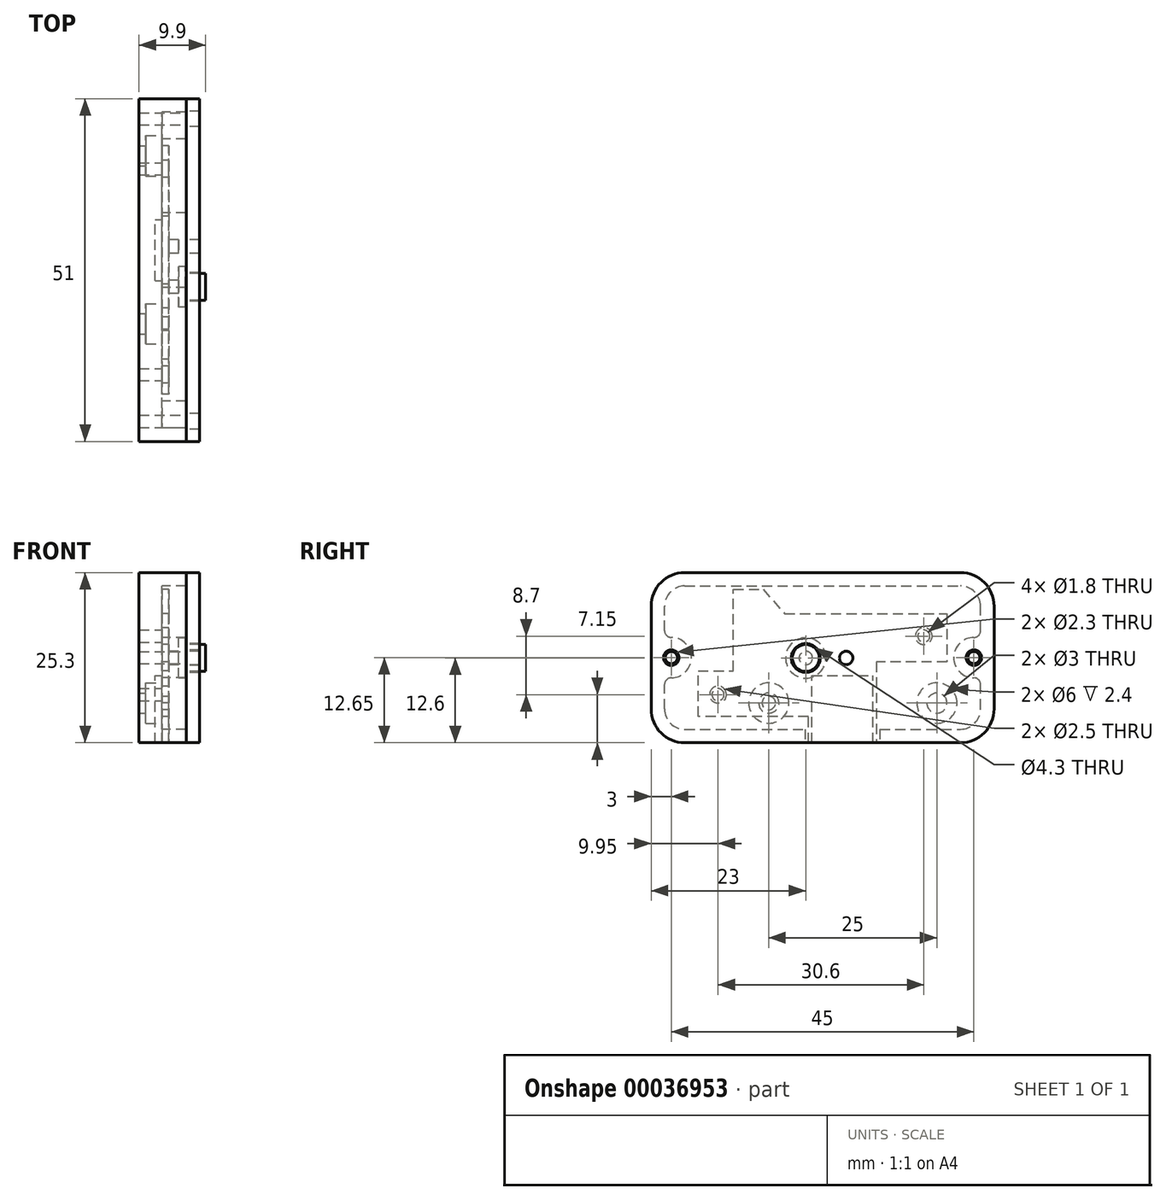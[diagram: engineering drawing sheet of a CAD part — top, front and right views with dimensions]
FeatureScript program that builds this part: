
annotation { "Feature Type Name" : "Feature", "Feature Type Description" : "" }
export const myFeature = defineFeature(function(context is Context, id is Id, definition is map)
    precondition{}
    {
        {
            var Q0;
            Q0=qCreatedBy(makeId("Right.planeOp"),FACE);
            var sketch = newSketch(context, id + "F0", { "sketchPlane" : qUnion([Q0])});
            skLineSegment(sketch, "E0", {"start": v(0, 0) * mm, "end": v(0, 6.8) * mm});
            skLineSegment(sketch, "E1", {"start": v(0, 6.8) * mm, "end": v(5.25, 6.8) * mm});
            skLineSegment(sketch, "E2", {"start": v(5.25, 6.8) * mm, "end": v(5.25, 18.9) * mm});
            skLineSegment(sketch, "E3", {"start": v(5.25, 18.9) * mm, "end": v(9.65, 18.9) * mm});
            skLineSegment(sketch, "E4", {"start": v(9.65, 18.9) * mm, "end": v(12.85, 15.3) * mm});
            skLineSegment(sketch, "E5", {"start": v(12.85, 15.3) * mm, "end": v(37, 15.3) * mm});
            skLineSegment(sketch, "E6", {"start": v(37, 15.3) * mm, "end": v(37, 8.1) * mm});
            skLineSegment(sketch, "E7", {"start": v(37, 8.1) * mm, "end": v(26.5, 8.1) * mm});
            skLineSegment(sketch, "E8", {"start": v(26.5, 8.1) * mm, "end": v(26.5, -3.9) * mm});
            skLineSegment(sketch, "E9", {"start": v(26.5, -3.9) * mm, "end": v(16.4, -3.9) * mm});
            skLineSegment(sketch, "E10", {"start": v(16.4, -3.9) * mm, "end": v(16.4, 0) * mm});
            skLineSegment(sketch, "E11", {"start": v(16.4, 0) * mm, "end": v(0, 0) * mm});
            skCircle(sketch, "E12", {"center": v(2.95, 3.25) * mm, "radius": 1.25 * mm});
            skCircle(sketch, "E13", {"center": v(10.5, 2) * mm, "radius": 1 * mm});
            skCircle(sketch, "E14", {"center": v(33.55, 11.95) * mm, "radius": 1.25 * mm});
            skSolve(sketch);
        }
        {
            var Q0;
            Q0 = qSketchRegion(id + "F0", true);
            extrude(context, id + "F1", {"entities" : qUnion([Q0]), "depth" : 1 * mm});
        }
        {
            var Q0;
            Q0=makeQuery(id+"F1.opExtrude","CAP_FACE",FACE,{"disambiguationData":[OSD([sQuery(id+"F0.wireOp",EDGE,"E0"),sQuery(id+"F0.wireOp",EDGE,"E1"),sQuery(id+"F0.wireOp",EDGE,"E2"),sQuery(id+"F0.wireOp",EDGE,"E3"),sQuery(id+"F0.wireOp",EDGE,"E4"),sQuery(id+"F0.wireOp",EDGE,"E5"),sQuery(id+"F0.wireOp",EDGE,"E6"),sQuery(id+"F0.wireOp",EDGE,"E7"),sQuery(id+"F0.wireOp",EDGE,"E8"),sQuery(id+"F0.wireOp",EDGE,"E9"),sQuery(id+"F0.wireOp",EDGE,"E10"),sQuery(id+"F0.wireOp",EDGE,"E11"),sQuery(id+"F0.wireOp",EDGE,"E12"),sQuery(id+"F0.wireOp",EDGE,"E13"),sQuery(id+"F0.wireOp",EDGE,"E14")])],"isStart":false});
            var sketch = newSketch(context, id + "F2", { "sketchPlane" : qUnion([Q0])});
            skCircle(sketch, "E15", {"center": v(16, 8.7) * mm, "radius": 1 * mm});
            skCircle(sketch, "E16", {"center": v(22, 8.7) * mm, "radius": 1 * mm});
            skSolve(sketch);
        }
        {
            var Q0;
            Q0 = qSketchRegion(id + "F2", true);
            extrude(context, id + "F3", {"entities" : qUnion([Q0]), "operationType" : NewBodyOperationType.ADD, "depth" : 1.5 * mm});
        }
        {
            var Q0;
            Q0=qCreatedBy(makeId("Right.planeOp"),FACE);
            var sketch = newSketch(context, id + "F4", { "sketchPlane" : qUnion([Q0])});
            skCircle(sketch, "E17.0", {"center": v(10.5, 2) * mm, "radius": 1 * mm});
            skCircle(sketch, "E18", {"center": v(10.5, 2) * mm, "radius": 1.5 * mm});
            skCircle(sketch, "E19", {"center": v(35.5, 2) * mm, "radius": 1.5 * mm});
            skLineSegment(sketch, "E20.bottom", {"start": v(-2, -3.9) * mm, "end": v(39, -3.9) * mm});
            skLineSegment(sketch, "E20.top", {"start": v(-2, 21.4) * mm, "end": v(39, 21.4) * mm});
            skLineSegment(sketch, "E20.left", {"start": v(-7, 1.1) * mm, "end": v(-7, 16.4) * mm});
            skLineSegment(sketch, "E20.right", {"start": v(44, 1.1) * mm, "end": v(44, 16.4) * mm});
            skPoint(sketch, "E21.visualSharp", {"position": v(-7, 21.4) * mm});
            skArc(sketch, "E21.filletArc", {"start": v(-2, 21.4) * mm, "mid": v(-5.54, 19.94) * mm, "end": v(-7, 16.4) * mm});
            skPoint(sketch, "E22.visualSharp", {"position": v(44, 21.4) * mm});
            skArc(sketch, "E22.filletArc", {"start": v(44, 16.4) * mm, "mid": v(42.54, 19.94) * mm, "end": v(39, 21.4) * mm});
            skPoint(sketch, "E23.visualSharp", {"position": v(44, -3.9) * mm});
            skArc(sketch, "E23.filletArc", {"start": v(39, -3.9) * mm, "mid": v(42.54, -2.44) * mm, "end": v(44, 1.1) * mm});
            skPoint(sketch, "E24.visualSharp", {"position": v(-7, -3.9) * mm});
            skArc(sketch, "E24.filletArc", {"start": v(-7, 1.1) * mm, "mid": v(-5.54, -2.44) * mm, "end": v(-2, -3.9) * mm});
            skSolve(sketch);
        }
        {
            var Q0;
            Q0=makeQuery(id+"F4.imprint","IMPRINT",FACE,{"disambiguationData":[TD([[makeQuery(id+"F4.imprint","IMPRINT",EDGE,{"derivedFrom":sQuery(id+"F4.wireOp",EDGE,"E18")}),-1.0]])]});
            extrude(context, id + "F5", {"entities" : qUnion([Q0]), "oppositeDirection" : true, "depth" : 3.4 * mm});
        }
        {
            var Q0;
            {var subQ0=sQuery(id+"F4.wireOp",EDGE,"E19");var subQ1=sQuery(id+"F4.wireOp",EDGE,"E20.bottom");var subQ2=sQuery(id+"F4.wireOp",EDGE,"E20.top");var subQ3=sQuery(id+"F4.wireOp",EDGE,"E20.left");var subQ4=sQuery(id+"F4.wireOp",EDGE,"E20.right");var subQ5=sQuery(id+"F4.wireOp",EDGE,"E21.filletArc");var subQ6=sQuery(id+"F4.wireOp",EDGE,"E22.filletArc");var subQ7=sQuery(id+"F4.wireOp",EDGE,"E23.filletArc");var subQ8=sQuery(id+"F4.wireOp",EDGE,"E24.filletArc");Q0=makeQuery(id+"F5.boolean.opBoolean","SPLIT",FACE,{"disambiguationData":[TD([makeQuery(id+"F1.opExtrude","SWEPT_FACE",FACE,{"disambiguationData":[OSD([sQuery(id+"F0.wireOp",EDGE,"E0")])]})])],"derivedFrom":makeQuery(id+"F5.opExtrude","CAP_FACE",FACE,{"disambiguationData":[OSD([sQuery(id+"F4.wireOp",EDGE,"E18"),subQ0,subQ1,subQ2,subQ3,subQ4,subQ5,subQ6,subQ7,subQ8])],"isStart":true})});}
            var sketch = newSketch(context, id + "F6", { "sketchPlane" : qUnion([Q0])});
            skCircle(sketch, "E25", {"center": v(35.5, 2) * mm, "radius": 3 * mm});
            skCircle(sketch, "E26", {"center": v(10.5, 2) * mm, "radius": 3 * mm});
            skSolve(sketch);
        }
        {
            var Q0;
            Q0 = qSketchRegion(id + "F6", true);
            extrude(context, id + "F7", {"entities" : qUnion([Q0]), "operationType" : NewBodyOperationType.REMOVE, "oppositeDirection" : true, "depth" : 2.4 * mm});
        }
        {
            var Q0;
            Q0=makeQuery(id+"F5.opExtrude","CAP_FACE",FACE,{"disambiguationData":[OSD([sQuery(id+"F4.wireOp",EDGE,"E18"),sQuery(id+"F4.wireOp",EDGE,"E19"),sQuery(id+"F4.wireOp",EDGE,"E20.bottom"),sQuery(id+"F4.wireOp",EDGE,"E20.top"),sQuery(id+"F4.wireOp",EDGE,"E20.left"),sQuery(id+"F4.wireOp",EDGE,"E20.right"),sQuery(id+"F4.wireOp",EDGE,"E21.filletArc"),sQuery(id+"F4.wireOp",EDGE,"E22.filletArc"),sQuery(id+"F4.wireOp",EDGE,"E23.filletArc"),sQuery(id+"F4.wireOp",EDGE,"E24.filletArc")])],"isStart":true});
            var sketch = newSketch(context, id + "F8", { "sketchPlane" : qUnion([Q0])});
            skLineSegment(sketch, "E27.bottom", {"start": v(16.9, -3.9) * mm, "end": v(26, -3.9) * mm});
            skLineSegment(sketch, "E27.top", {"start": v(16.9, 6.1) * mm, "end": v(26, 6.1) * mm});
            skLineSegment(sketch, "E27.left", {"start": v(16.9, -3.9) * mm, "end": v(16.9, 6.1) * mm});
            skLineSegment(sketch, "E27.right", {"start": v(26, -3.9) * mm, "end": v(26, 6.1) * mm});
            skSolve(sketch);
        }
        {
            var Q0;
            Q0 = qSketchRegion(id + "F8", true);
            extrude(context, id + "F9", {"entities" : qUnion([Q0]), "operationType" : NewBodyOperationType.REMOVE, "oppositeDirection" : true, "depth" : 1 * mm});
        }
        {
            var Q0;
            Q0=makeQuery(id+"F5.opExtrude","CAP_FACE",FACE,{"disambiguationData":[OSD([sQuery(id+"F4.wireOp",EDGE,"E18"),sQuery(id+"F4.wireOp",EDGE,"E19"),sQuery(id+"F4.wireOp",EDGE,"E20.bottom"),sQuery(id+"F4.wireOp",EDGE,"E20.top"),sQuery(id+"F4.wireOp",EDGE,"E20.left"),sQuery(id+"F4.wireOp",EDGE,"E20.right"),sQuery(id+"F4.wireOp",EDGE,"E21.filletArc"),sQuery(id+"F4.wireOp",EDGE,"E22.filletArc"),sQuery(id+"F4.wireOp",EDGE,"E23.filletArc"),sQuery(id+"F4.wireOp",EDGE,"E24.filletArc")])],"isStart":true});
            var sketch = newSketch(context, id + "F10", { "sketchPlane" : qUnion([Q0])});
            skCircle(sketch, "E28", {"center": v(33.55, 11.95) * mm, "radius": 0.9 * mm});
            skCircle(sketch, "E29", {"center": v(2.95, 3.25) * mm, "radius": 0.9 * mm});
            skSolve(sketch);
        }
        {
            var Q0;
            Q0 = qSketchRegion(id + "F10", true);
            extrude(context, id + "F11", {"entities" : qUnion([Q0]), "operationType" : NewBodyOperationType.REMOVE, "endBound" : BoundingType.THROUGH_ALL, "oppositeDirection" : true, "depth" : 25 * mm});
        }
        {
            var Q0;
            Q0=makeQuery(id+"F5.opExtrude","CAP_FACE",FACE,{"disambiguationData":[OSD([sQuery(id+"F4.wireOp",EDGE,"E18"),sQuery(id+"F4.wireOp",EDGE,"E19"),sQuery(id+"F4.wireOp",EDGE,"E20.bottom"),sQuery(id+"F4.wireOp",EDGE,"E20.top"),sQuery(id+"F4.wireOp",EDGE,"E20.left"),sQuery(id+"F4.wireOp",EDGE,"E20.right"),sQuery(id+"F4.wireOp",EDGE,"E21.filletArc"),sQuery(id+"F4.wireOp",EDGE,"E22.filletArc"),sQuery(id+"F4.wireOp",EDGE,"E23.filletArc"),sQuery(id+"F4.wireOp",EDGE,"E24.filletArc")])],"isStart":true});
            var sketch = newSketch(context, id + "F12", { "sketchPlane" : qUnion([Q0])});
            skLineSegment(sketch, "E30.0", {"start": v(-2, 21.4) * mm, "end": v(39, 21.4) * mm});
            skArc(sketch, "E31.0", {"start": v(44, 16.4) * mm, "mid": v(42.54, 19.94) * mm, "end": v(39, 21.4) * mm});
            skLineSegment(sketch, "E32.0", {"start": v(44, 1.1) * mm, "end": v(44, 16.4) * mm});
            skArc(sketch, "E33.0", {"start": v(39, -3.9) * mm, "mid": v(42.54, -2.44) * mm, "end": v(44, 1.1) * mm});
            skLineSegment(sketch, "E34.0", {"start": v(26, -3.9) * mm, "end": v(39, -3.9) * mm});
            skLineSegment(sketch, "E35.0", {"start": v(-2, -3.9) * mm, "end": v(16.9, -3.9) * mm});
            skArc(sketch, "E36.0", {"start": v(-7, 1.1) * mm, "mid": v(-5.54, -2.44) * mm, "end": v(-2, -3.9) * mm});
            skLineSegment(sketch, "E37.0", {"start": v(-7, 1.1) * mm, "end": v(-7, 16.4) * mm});
            skArc(sketch, "E38.0", {"start": v(-2, 21.4) * mm, "mid": v(-5.54, 19.94) * mm, "end": v(-7, 16.4) * mm});
            skLineSegment(sketch, "E39.0", {"start": v(27, -1.9) * mm, "end": v(39, -1.9) * mm});
            skArc(sketch, "E39.1", {"start": v(39, -1.9) * mm, "mid": v(41.12, -1.02) * mm, "end": v(42, 1.1) * mm});
            skLineSegment(sketch, "E39.2", {"start": v(42, 1.1) * mm, "end": v(42, 4.75) * mm});
            skArc(sketch, "E39.3", {"start": v(42, 16.4) * mm, "mid": v(41.12, 18.52) * mm, "end": v(39, 19.4) * mm});
            skLineSegment(sketch, "E39.4", {"start": v(-2, 19.4) * mm, "end": v(39, 19.4) * mm});
            skArc(sketch, "E39.5", {"start": v(-2, 19.4) * mm, "mid": v(-4.12, 18.52) * mm, "end": v(-5, 16.4) * mm});
            skLineSegment(sketch, "E39.6", {"start": v(-5, 1.1) * mm, "end": v(-5, 4.75) * mm});
            skArc(sketch, "E39.7", {"start": v(-5, 1.1) * mm, "mid": v(-4.12, -1.02) * mm, "end": v(-2, -1.9) * mm});
            skLineSegment(sketch, "E39.8", {"start": v(-2, -1.9) * mm, "end": v(15.9, -1.9) * mm});
            skLineSegment(sketch, "E40", {"start": v(15.9, -1.9) * mm, "end": v(15.9, -3.9) * mm});
            skLineSegment(sketch, "E41", {"start": v(27, -1.9) * mm, "end": v(27, -3.9) * mm});
            skArc(sketch, "E42", {"start": v(-4, 5.75) * mm, "mid": v(-1, 8.75) * mm, "end": v(-4, 11.75) * mm});
            skArc(sketch, "E43", {"start": v(-5, 12.75) * mm, "mid": v(-4.7, 12.04) * mm, "end": v(-4, 11.75) * mm});
            skArc(sketch, "E44", {"start": v(-4, 5.75) * mm, "mid": v(-4.7, 5.46) * mm, "end": v(-5, 4.75) * mm});
            skPoint(sketch, "E45", {"position": v(-7, 8.75) * mm});
            skLineSegment(sketch, "E46.trimOffspring", {"start": v(-5, 12.75) * mm, "end": v(-5, 16.4) * mm});
            skArc(sketch, "E47", {"start": v(41, 11.75) * mm, "mid": v(38, 8.75) * mm, "end": v(41, 5.75) * mm});
            skArc(sketch, "E48", {"start": v(41, 11.75) * mm, "mid": v(41.7, 12.04) * mm, "end": v(42, 12.75) * mm});
            skArc(sketch, "E49", {"start": v(42, 4.75) * mm, "mid": v(41.7, 5.46) * mm, "end": v(41, 5.75) * mm});
            skPoint(sketch, "E50", {"position": v(44, 8.75) * mm});
            skLineSegment(sketch, "E51.trimOffspring", {"start": v(42, 12.75) * mm, "end": v(42, 16.4) * mm});
            skSolve(sketch);
        }
        {
            var Q0;
            Q0 = qSketchRegion(id + "F12", true);
            extrude(context, id + "F13", {"entities" : qUnion([Q0]), "operationType" : NewBodyOperationType.ADD, "depth" : 3.6 * mm});
        }
        {
            var Q0;
            Q0=makeQuery(id+"F13.opExtrude","CAP_FACE",FACE,{"disambiguationData":[OSD([sQuery(id+"F12.wireOp",EDGE,"E30.0"),sQuery(id+"F12.wireOp",EDGE,"E31.0"),sQuery(id+"F12.wireOp",EDGE,"E32.0"),sQuery(id+"F12.wireOp",EDGE,"E33.0"),sQuery(id+"F12.wireOp",EDGE,"E34.0"),sQuery(id+"F12.wireOp",EDGE,"E35.0"),sQuery(id+"F12.wireOp",EDGE,"E36.0"),sQuery(id+"F12.wireOp",EDGE,"E37.0"),sQuery(id+"F12.wireOp",EDGE,"E38.0"),sQuery(id+"F12.wireOp",EDGE,"E39.0"),sQuery(id+"F12.wireOp",EDGE,"E39.1"),sQuery(id+"F12.wireOp",EDGE,"E39.2"),sQuery(id+"F12.wireOp",EDGE,"E39.3"),sQuery(id+"F12.wireOp",EDGE,"E39.4"),sQuery(id+"F12.wireOp",EDGE,"E39.5"),sQuery(id+"F12.wireOp",EDGE,"E39.6"),sQuery(id+"F12.wireOp",EDGE,"E39.7"),sQuery(id+"F12.wireOp",EDGE,"E39.8"),sQuery(id+"F12.wireOp",EDGE,"E40"),sQuery(id+"F12.wireOp",EDGE,"E41"),sQuery(id+"F12.wireOp",EDGE,"E42"),sQuery(id+"F12.wireOp",EDGE,"E43"),sQuery(id+"F12.wireOp",EDGE,"E44"),sQuery(id+"F12.wireOp",EDGE,"E46.trimOffspring"),sQuery(id+"F12.wireOp",EDGE,"E47"),sQuery(id+"F12.wireOp",EDGE,"E48"),sQuery(id+"F12.wireOp",EDGE,"E49"),sQuery(id+"F12.wireOp",EDGE,"E51.trimOffspring")])],"isStart":false});
            var sketch = newSketch(context, id + "F14", { "sketchPlane" : qUnion([Q0])});
            skCircle(sketch, "E52", {"center": v(-4, 8.75) * mm, "radius": 0.9 * mm});
            skCircle(sketch, "E53", {"center": v(41, 8.75) * mm, "radius": 0.9 * mm});
            skSolve(sketch);
        }
        {
            var Q0;
            Q0 = qSketchRegion(id + "F14", true);
            extrude(context, id + "F15", {"entities" : qUnion([Q0]), "operationType" : NewBodyOperationType.REMOVE, "endBound" : BoundingType.THROUGH_ALL, "oppositeDirection" : true, "depth" : 25 * mm});
        }
        {
            var Q0;
            Q0=makeQuery(id+"F13.opExtrude","CAP_FACE",FACE,{"disambiguationData":[OSD([sQuery(id+"F12.wireOp",EDGE,"E30.0"),sQuery(id+"F12.wireOp",EDGE,"E31.0"),sQuery(id+"F12.wireOp",EDGE,"E32.0"),sQuery(id+"F12.wireOp",EDGE,"E33.0"),sQuery(id+"F12.wireOp",EDGE,"E34.0"),sQuery(id+"F12.wireOp",EDGE,"E35.0"),sQuery(id+"F12.wireOp",EDGE,"E36.0"),sQuery(id+"F12.wireOp",EDGE,"E37.0"),sQuery(id+"F12.wireOp",EDGE,"E38.0"),sQuery(id+"F12.wireOp",EDGE,"E39.0"),sQuery(id+"F12.wireOp",EDGE,"E39.1"),sQuery(id+"F12.wireOp",EDGE,"E39.2"),sQuery(id+"F12.wireOp",EDGE,"E39.3"),sQuery(id+"F12.wireOp",EDGE,"E39.4"),sQuery(id+"F12.wireOp",EDGE,"E39.5"),sQuery(id+"F12.wireOp",EDGE,"E39.6"),sQuery(id+"F12.wireOp",EDGE,"E39.7"),sQuery(id+"F12.wireOp",EDGE,"E39.8"),sQuery(id+"F12.wireOp",EDGE,"E40"),sQuery(id+"F12.wireOp",EDGE,"E41"),sQuery(id+"F12.wireOp",EDGE,"E42"),sQuery(id+"F12.wireOp",EDGE,"E43"),sQuery(id+"F12.wireOp",EDGE,"E44"),sQuery(id+"F12.wireOp",EDGE,"417ee6bc-ae09-479d-8291-56012da80ed6"),sQuery(id+"F12.wireOp",EDGE,"E46.trimOffspring"),sQuery(id+"F12.wireOp",EDGE,"E47"),sQuery(id+"F12.wireOp",EDGE,"E48"),sQuery(id+"F12.wireOp",EDGE,"E49"),sQuery(id+"F12.wireOp",EDGE,"E51.trimOffspring"),sQuery(id+"F12.wireOp",EDGE,"95503bac-c556-4579-a5fb-9d73f4b7cb5d")])],"isStart":false});
            var sketch = newSketch(context, id + "F16", { "sketchPlane" : qUnion([Q0])});
            skLineSegment(sketch, "E54.0", {"start": v(-7, 1.1) * mm, "end": v(-7, 16.4) * mm});
            skArc(sketch, "E54.1", {"start": v(-2, 21.4) * mm, "mid": v(-5.54, 19.94) * mm, "end": v(-7, 16.4) * mm});
            skLineSegment(sketch, "E54.2", {"start": v(-2, 21.4) * mm, "end": v(39, 21.4) * mm});
            skArc(sketch, "E54.3", {"start": v(44, 16.4) * mm, "mid": v(42.54, 19.94) * mm, "end": v(39, 21.4) * mm});
            skLineSegment(sketch, "E54.4", {"start": v(44, 1.1) * mm, "end": v(44, 16.4) * mm});
            skArc(sketch, "E54.5", {"start": v(39, -3.9) * mm, "mid": v(42.54, -2.44) * mm, "end": v(44, 1.1) * mm});
            skLineSegment(sketch, "E54.6", {"start": v(27, -3.9) * mm, "end": v(39, -3.9) * mm});
            skLineSegment(sketch, "E54.7", {"start": v(-2, -3.9) * mm, "end": v(15.9, -3.9) * mm});
            skArc(sketch, "E54.8", {"start": v(-7, 1.1) * mm, "mid": v(-5.54, -2.44) * mm, "end": v(-2, -3.9) * mm});
            skLineSegment(sketch, "E55", {"start": v(15.9, -3.9) * mm, "end": v(27, -3.9) * mm});
            skCircle(sketch, "E56", {"center": v(-4, 8.75) * mm, "radius": 1.15 * mm});
            skCircle(sketch, "E57", {"center": v(41, 8.75) * mm, "radius": 1.15 * mm});
            skCircle(sketch, "E58.0", {"center": v(16, 8.7) * mm, "radius": 1 * mm});
            skCircle(sketch, "E59", {"center": v(16, 8.7) * mm, "radius": 2.15 * mm});
            skCircle(sketch, "E60.0", {"center": v(22, 8.7) * mm, "radius": 1 * mm});
            skSolve(sketch);
        }
        {
            var Q0;
            Q0 = qSketchRegion(id + "F16", true);
            extrude(context, id + "F17", {"entities" : qUnion([Q0]), "depth" : 2 * mm});
        }
        {
            var Q0;
            Q0=makeQuery(id+"F3.opExtrude","CAP_FACE",FACE,{"disambiguationData":[OSD([sQuery(id+"F2.wireOp",EDGE,"E15")])],"isStart":false});
            var sketch = newSketch(context, id + "F18", { "sketchPlane" : qUnion([Q0])});
            skCircle(sketch, "E61", {"center": v(16, 8.7) * mm, "radius": 3 * mm});
            skSolve(sketch);
        }
        {
            var Q0;
            Q0 = qSketchRegion(id + "F18", true);
            extrude(context, id + "F19", {"entities" : qUnion([Q0]), "depth" : 1 * mm});
        }
        {
            var Q0;
            Q0=makeQuery(id+"F19.opExtrude","CAP_FACE",FACE,{"disambiguationData":[OSD([sQuery(id+"F18.wireOp",EDGE,"E61")])],"isStart":false});
            var sketch = newSketch(context, id + "F20", { "sketchPlane" : qUnion([Q0])});
            skCircle(sketch, "E62", {"center": v(16, 8.7) * mm, "radius": 2 * mm});
            skSolve(sketch);
        }
        {
            var Q0;
            Q0 = qSketchRegion(id + "F20", true);
            extrude(context, id + "F21", {"entities" : qUnion([Q0]), "operationType" : NewBodyOperationType.ADD, "depth" : 3 * mm});
        }
    });
